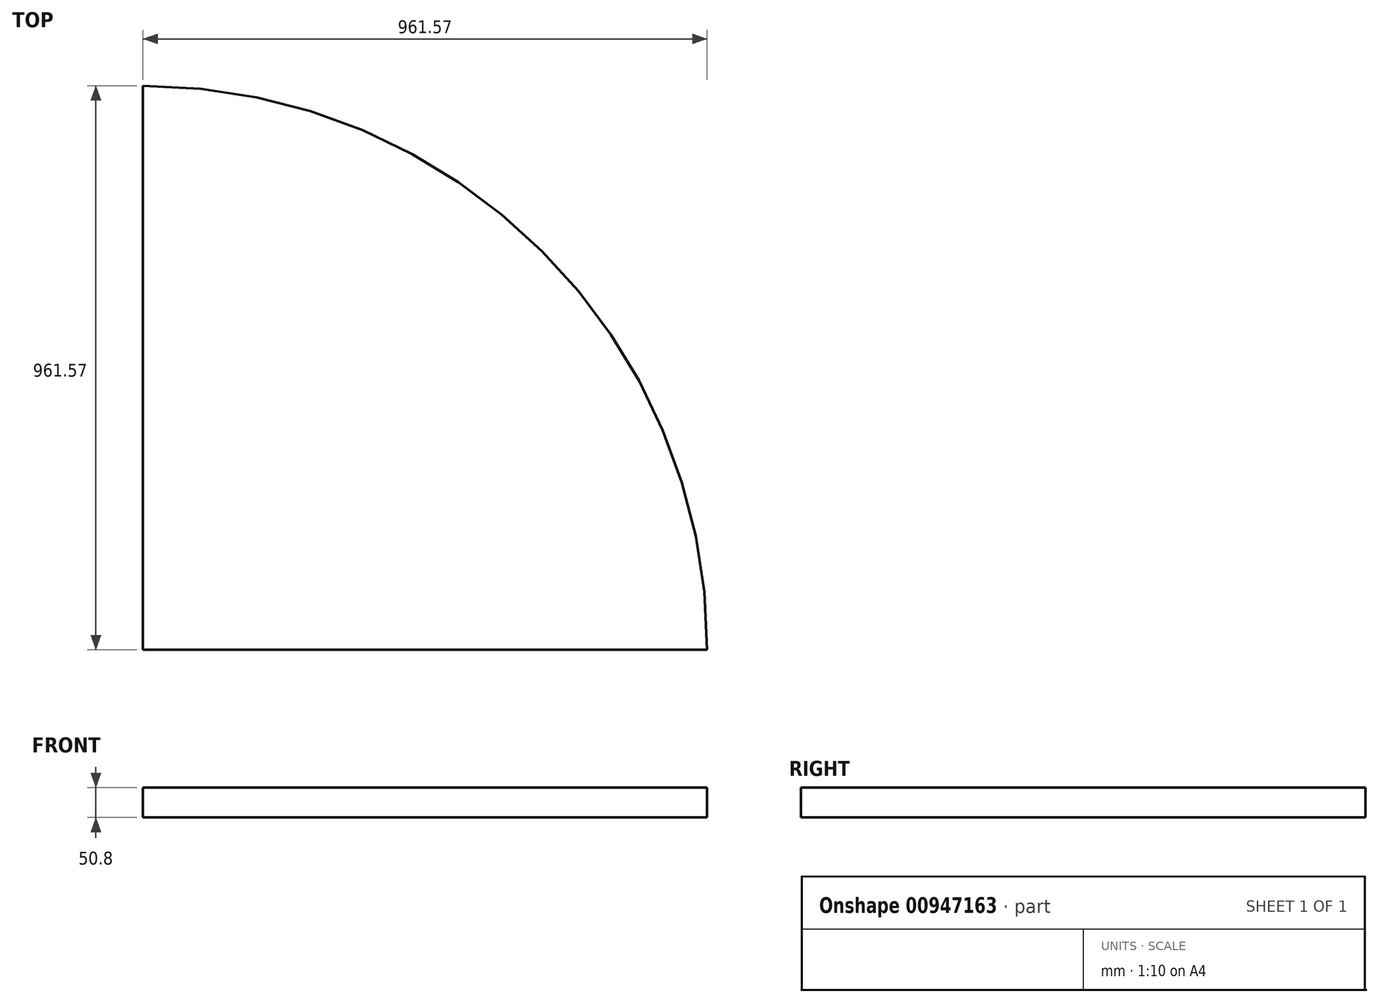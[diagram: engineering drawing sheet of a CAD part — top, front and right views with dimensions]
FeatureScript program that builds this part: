
annotation { "Feature Type Name" : "Feature", "Feature Type Description" : "" }
export const myFeature = defineFeature(function(context is Context, id is Id, definition is map)
    precondition{}
    {
        {
            var Q0;
            Q0=qCreatedBy(makeId("Top.planeOp"),FACE);
            var sketch = newSketch(context, id + "F0", { "sketchPlane" : qUnion([Q0])});
            skLineSegment(sketch, "E0.bottom", {"start": v(0, 0) * mm, "end": v(965.2, 0) * mm});
            skLineSegment(sketch, "E0.top", {"start": v(0, 965.2) * mm, "end": v(965.2, 965.2) * mm});
            skLineSegment(sketch, "E0.left", {"start": v(0, 0) * mm, "end": v(0, 965.2) * mm});
            skLineSegment(sketch, "E0.right", {"start": v(965.2, 0) * mm, "end": v(965.2, 965.2) * mm});
            skArc(sketch, "E1", {"start": v(961.57, 0) * mm, "mid": v(679.93, 679.93) * mm, "end": v(0, 961.57) * mm});
            skSolve(sketch);
        }
        {
            var Q0;
            {var subQ3=sQuery(id+"F0.wireOp",EDGE,"E1");Q0=makeQuery(id+"F0.imprint","IMPRINT",FACE,{"disambiguationData":[TD([[makeQuery(id+"F0.imprint","IMPRINT",EDGE,{"derivedFrom":subQ3}),1.0]])]});}
            extrude(context, id + "F1", {"entities" : qUnion([Q0]), "depth" : 50.8 * mm, "offsetDistance" : 25.4 * mm});
        }
    });
